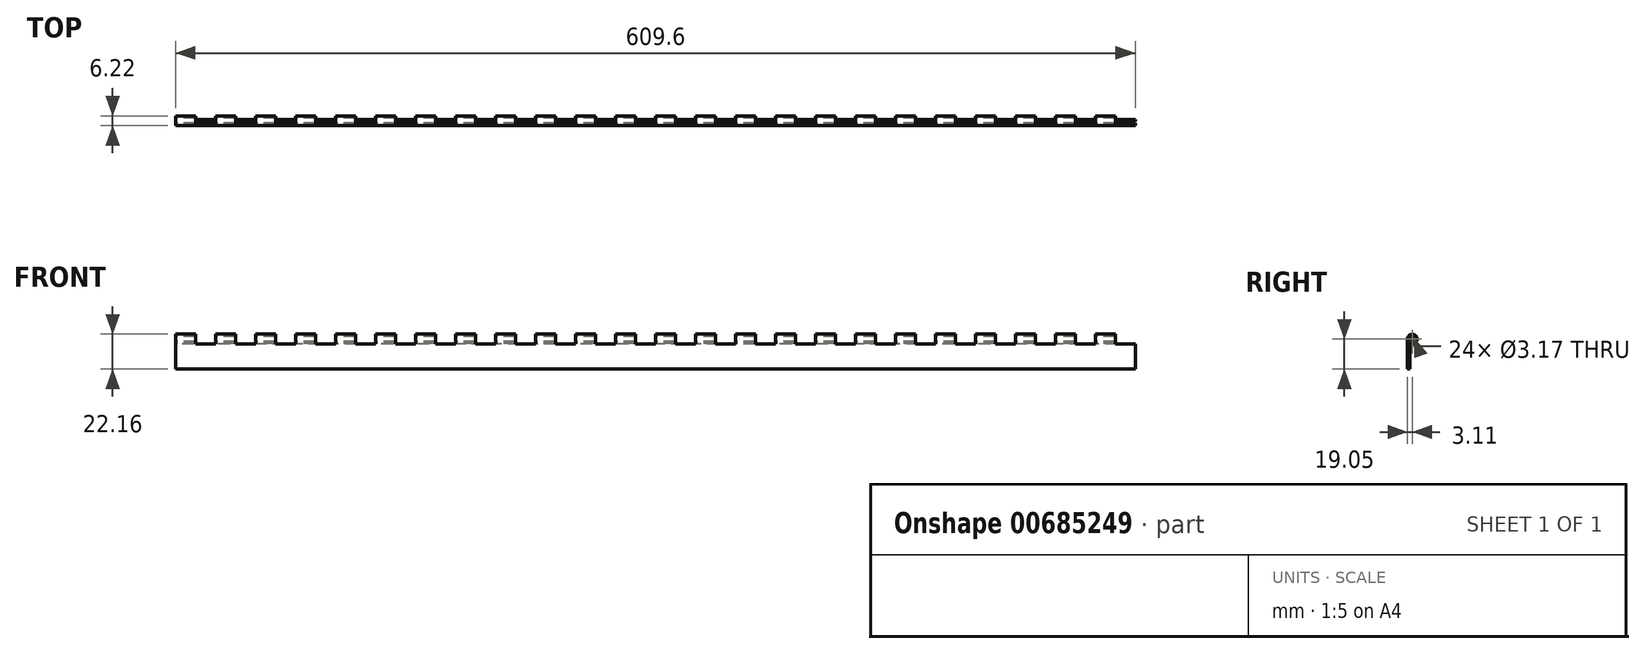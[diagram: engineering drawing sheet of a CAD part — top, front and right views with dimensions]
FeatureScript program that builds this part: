
annotation { "Feature Type Name" : "Feature", "Feature Type Description" : "" }
export const myFeature = defineFeature(function(context is Context, id is Id, definition is map)
    precondition{}
    {
        {
            var Q0;
            Q0=qCreatedBy(makeId("Right.planeOp"),FACE);
            var sketch = newSketch(context, id + "F0", { "sketchPlane" : qUnion([Q0])});
            skCircle(sketch, "E0", {"center": v(0, 0) * mm, "radius": 1.59 * mm});
            skArc(sketch, "E1", {"start": v(-1.59, -2.68) * mm, "mid": v(2.7, 1.54) * mm, "end": v(-3.11, 0) * mm});
            skLineSegment(sketch, "E2.top", {"start": v(-3.11, -19.05) * mm, "end": v(-1.59, -19.05) * mm});
            skLineSegment(sketch, "E2.left", {"start": v(-3.11, 0) * mm, "end": v(-3.11, -19.05) * mm});
            skLineSegment(sketch, "E2.right", {"start": v(-1.59, -2.68) * mm, "end": v(-1.59, -19.05) * mm});
            skSolve(sketch);
        }
        {
            var Q0;
            Q0 = qSketchRegion(id + "F0", true);
            extrude(context, id + "F1", {"entities" : qUnion([Q0]), "depth" : 609.6 * mm, "offsetDistance" : 25.4 * mm});
        }
        {
            var Q0;
            Q0=qCreatedBy(makeId("Front.planeOp"),FACE);
            var sketch = newSketch(context, id + "F2", { "sketchPlane" : qUnion([Q0])});
            skLineSegment(sketch, "E3.bottom", {"start": v(12.7, 3.18) * mm, "end": v(25.4, 3.18) * mm});
            skLineSegment(sketch, "E3.top", {"start": v(12.7, -3.05) * mm, "end": v(25.4, -3.05) * mm});
            skLineSegment(sketch, "E3.left", {"start": v(12.7, 3.18) * mm, "end": v(12.7, -3.05) * mm});
            skLineSegment(sketch, "E3.right", {"start": v(25.4, 3.18) * mm, "end": v(25.4, -3.05) * mm});
            skLineSegment(sketch, "E4.1.0.0", {"start": v(38.1, 3.18) * mm, "end": v(50.8, 3.18) * mm});
            skLineSegment(sketch, "E4.1.0.1", {"start": v(50.8, 3.18) * mm, "end": v(50.8, -3.05) * mm});
            skLineSegment(sketch, "E4.1.0.2", {"start": v(38.1, -3.05) * mm, "end": v(50.8, -3.05) * mm});
            skLineSegment(sketch, "E4.1.0.3", {"start": v(38.1, 3.18) * mm, "end": v(38.1, -3.05) * mm});
            skLineSegment(sketch, "E4.2.0.0", {"start": v(63.5, 3.18) * mm, "end": v(76.2, 3.18) * mm});
            skLineSegment(sketch, "E4.2.0.1", {"start": v(76.2, 3.18) * mm, "end": v(76.2, -3.05) * mm});
            skLineSegment(sketch, "E4.2.0.2", {"start": v(63.5, -3.05) * mm, "end": v(76.2, -3.05) * mm});
            skLineSegment(sketch, "E4.2.0.3", {"start": v(63.5, 3.18) * mm, "end": v(63.5, -3.05) * mm});
            skLineSegment(sketch, "E4.3.0.0", {"start": v(88.9, 3.18) * mm, "end": v(101.6, 3.18) * mm});
            skLineSegment(sketch, "E4.3.0.1", {"start": v(101.6, 3.18) * mm, "end": v(101.6, -3.05) * mm});
            skLineSegment(sketch, "E4.3.0.2", {"start": v(88.9, -3.05) * mm, "end": v(101.6, -3.05) * mm});
            skLineSegment(sketch, "E4.3.0.3", {"start": v(88.9, 3.18) * mm, "end": v(88.9, -3.05) * mm});
            skLineSegment(sketch, "E4.4.0.0", {"start": v(114.3, 3.18) * mm, "end": v(127, 3.18) * mm});
            skLineSegment(sketch, "E4.4.0.1", {"start": v(127, 3.18) * mm, "end": v(127, -3.05) * mm});
            skLineSegment(sketch, "E4.4.0.2", {"start": v(114.3, -3.05) * mm, "end": v(127, -3.05) * mm});
            skLineSegment(sketch, "E4.4.0.3", {"start": v(114.3, 3.18) * mm, "end": v(114.3, -3.05) * mm});
            skLineSegment(sketch, "E4.5.0.0", {"start": v(139.7, 3.18) * mm, "end": v(152.4, 3.18) * mm});
            skLineSegment(sketch, "E4.5.0.1", {"start": v(152.4, 3.18) * mm, "end": v(152.4, -3.05) * mm});
            skLineSegment(sketch, "E4.5.0.2", {"start": v(139.7, -3.05) * mm, "end": v(152.4, -3.05) * mm});
            skLineSegment(sketch, "E4.5.0.3", {"start": v(139.7, 3.18) * mm, "end": v(139.7, -3.05) * mm});
            skLineSegment(sketch, "E4.6.0.0", {"start": v(165.1, 3.18) * mm, "end": v(177.8, 3.18) * mm});
            skLineSegment(sketch, "E4.6.0.1", {"start": v(177.8, 3.18) * mm, "end": v(177.8, -3.05) * mm});
            skLineSegment(sketch, "E4.6.0.2", {"start": v(165.1, -3.05) * mm, "end": v(177.8, -3.05) * mm});
            skLineSegment(sketch, "E4.6.0.3", {"start": v(165.1, 3.18) * mm, "end": v(165.1, -3.05) * mm});
            skLineSegment(sketch, "E4.7.0.0", {"start": v(190.5, 3.18) * mm, "end": v(203.2, 3.18) * mm});
            skLineSegment(sketch, "E4.7.0.1", {"start": v(203.2, 3.18) * mm, "end": v(203.2, -3.05) * mm});
            skLineSegment(sketch, "E4.7.0.2", {"start": v(190.5, -3.05) * mm, "end": v(203.2, -3.05) * mm});
            skLineSegment(sketch, "E4.7.0.3", {"start": v(190.5, 3.18) * mm, "end": v(190.5, -3.05) * mm});
            skLineSegment(sketch, "E4.8.0.0", {"start": v(215.9, 3.18) * mm, "end": v(228.6, 3.18) * mm});
            skLineSegment(sketch, "E4.8.0.1", {"start": v(228.6, 3.18) * mm, "end": v(228.6, -3.05) * mm});
            skLineSegment(sketch, "E4.8.0.2", {"start": v(215.9, -3.05) * mm, "end": v(228.6, -3.05) * mm});
            skLineSegment(sketch, "E4.8.0.3", {"start": v(215.9, 3.18) * mm, "end": v(215.9, -3.05) * mm});
            skLineSegment(sketch, "E4.9.0.0", {"start": v(241.3, 3.18) * mm, "end": v(254, 3.18) * mm});
            skLineSegment(sketch, "E4.9.0.1", {"start": v(254, 3.18) * mm, "end": v(254, -3.05) * mm});
            skLineSegment(sketch, "E4.9.0.2", {"start": v(241.3, -3.05) * mm, "end": v(254, -3.05) * mm});
            skLineSegment(sketch, "E4.9.0.3", {"start": v(241.3, 3.18) * mm, "end": v(241.3, -3.05) * mm});
            skLineSegment(sketch, "E4.10.0.0", {"start": v(266.7, 3.18) * mm, "end": v(279.4, 3.18) * mm});
            skLineSegment(sketch, "E4.10.0.1", {"start": v(279.4, 3.18) * mm, "end": v(279.4, -3.05) * mm});
            skLineSegment(sketch, "E4.10.0.2", {"start": v(266.7, -3.05) * mm, "end": v(279.4, -3.05) * mm});
            skLineSegment(sketch, "E4.10.0.3", {"start": v(266.7, 3.18) * mm, "end": v(266.7, -3.05) * mm});
            skLineSegment(sketch, "E4.11.0.0", {"start": v(292.1, 3.18) * mm, "end": v(304.8, 3.18) * mm});
            skLineSegment(sketch, "E4.11.0.1", {"start": v(304.8, 3.18) * mm, "end": v(304.8, -3.05) * mm});
            skLineSegment(sketch, "E4.11.0.2", {"start": v(292.1, -3.05) * mm, "end": v(304.8, -3.05) * mm});
            skLineSegment(sketch, "E4.11.0.3", {"start": v(292.1, 3.18) * mm, "end": v(292.1, -3.05) * mm});
            skLineSegment(sketch, "E4.12.0.0", {"start": v(317.5, 3.18) * mm, "end": v(330.2, 3.18) * mm});
            skLineSegment(sketch, "E4.12.0.1", {"start": v(330.2, 3.18) * mm, "end": v(330.2, -3.05) * mm});
            skLineSegment(sketch, "E4.12.0.2", {"start": v(317.5, -3.05) * mm, "end": v(330.2, -3.05) * mm});
            skLineSegment(sketch, "E4.12.0.3", {"start": v(317.5, 3.18) * mm, "end": v(317.5, -3.05) * mm});
            skLineSegment(sketch, "E4.13.0.0", {"start": v(342.9, 3.18) * mm, "end": v(355.6, 3.18) * mm});
            skLineSegment(sketch, "E4.13.0.1", {"start": v(355.6, 3.18) * mm, "end": v(355.6, -3.05) * mm});
            skLineSegment(sketch, "E4.13.0.2", {"start": v(342.9, -3.05) * mm, "end": v(355.6, -3.05) * mm});
            skLineSegment(sketch, "E4.13.0.3", {"start": v(342.9, 3.18) * mm, "end": v(342.9, -3.05) * mm});
            skLineSegment(sketch, "E4.14.0.0", {"start": v(368.3, 3.18) * mm, "end": v(381, 3.18) * mm});
            skLineSegment(sketch, "E4.14.0.1", {"start": v(381, 3.18) * mm, "end": v(381, -3.05) * mm});
            skLineSegment(sketch, "E4.14.0.2", {"start": v(368.3, -3.05) * mm, "end": v(381, -3.05) * mm});
            skLineSegment(sketch, "E4.14.0.3", {"start": v(368.3, 3.18) * mm, "end": v(368.3, -3.05) * mm});
            skLineSegment(sketch, "E4.15.0.0", {"start": v(393.7, 3.18) * mm, "end": v(406.4, 3.18) * mm});
            skLineSegment(sketch, "E4.15.0.1", {"start": v(406.4, 3.18) * mm, "end": v(406.4, -3.05) * mm});
            skLineSegment(sketch, "E4.15.0.2", {"start": v(393.7, -3.05) * mm, "end": v(406.4, -3.05) * mm});
            skLineSegment(sketch, "E4.15.0.3", {"start": v(393.7, 3.18) * mm, "end": v(393.7, -3.05) * mm});
            skLineSegment(sketch, "E4.16.0.0", {"start": v(419.1, 3.18) * mm, "end": v(431.8, 3.18) * mm});
            skLineSegment(sketch, "E4.16.0.1", {"start": v(431.8, 3.18) * mm, "end": v(431.8, -3.05) * mm});
            skLineSegment(sketch, "E4.16.0.2", {"start": v(419.1, -3.05) * mm, "end": v(431.8, -3.05) * mm});
            skLineSegment(sketch, "E4.16.0.3", {"start": v(419.1, 3.18) * mm, "end": v(419.1, -3.05) * mm});
            skLineSegment(sketch, "E4.17.0.0", {"start": v(444.5, 3.18) * mm, "end": v(457.2, 3.18) * mm});
            skLineSegment(sketch, "E4.17.0.1", {"start": v(457.2, 3.18) * mm, "end": v(457.2, -3.05) * mm});
            skLineSegment(sketch, "E4.17.0.2", {"start": v(444.5, -3.05) * mm, "end": v(457.2, -3.05) * mm});
            skLineSegment(sketch, "E4.17.0.3", {"start": v(444.5, 3.18) * mm, "end": v(444.5, -3.05) * mm});
            skLineSegment(sketch, "E4.18.0.0", {"start": v(469.9, 3.18) * mm, "end": v(482.6, 3.18) * mm});
            skLineSegment(sketch, "E4.18.0.1", {"start": v(482.6, 3.18) * mm, "end": v(482.6, -3.05) * mm});
            skLineSegment(sketch, "E4.18.0.2", {"start": v(469.9, -3.05) * mm, "end": v(482.6, -3.05) * mm});
            skLineSegment(sketch, "E4.18.0.3", {"start": v(469.9, 3.18) * mm, "end": v(469.9, -3.05) * mm});
            skLineSegment(sketch, "E4.19.0.0", {"start": v(495.3, 3.18) * mm, "end": v(508, 3.18) * mm});
            skLineSegment(sketch, "E4.19.0.1", {"start": v(508, 3.18) * mm, "end": v(508, -3.05) * mm});
            skLineSegment(sketch, "E4.19.0.2", {"start": v(495.3, -3.05) * mm, "end": v(508, -3.05) * mm});
            skLineSegment(sketch, "E4.19.0.3", {"start": v(495.3, 3.18) * mm, "end": v(495.3, -3.05) * mm});
            skLineSegment(sketch, "E4.20.0.0", {"start": v(520.7, 3.18) * mm, "end": v(533.4, 3.18) * mm});
            skLineSegment(sketch, "E4.20.0.1", {"start": v(533.4, 3.18) * mm, "end": v(533.4, -3.05) * mm});
            skLineSegment(sketch, "E4.20.0.2", {"start": v(520.7, -3.05) * mm, "end": v(533.4, -3.05) * mm});
            skLineSegment(sketch, "E4.20.0.3", {"start": v(520.7, 3.18) * mm, "end": v(520.7, -3.05) * mm});
            skLineSegment(sketch, "E4.21.0.0", {"start": v(546.1, 3.18) * mm, "end": v(558.8, 3.18) * mm});
            skLineSegment(sketch, "E4.21.0.1", {"start": v(558.8, 3.18) * mm, "end": v(558.8, -3.05) * mm});
            skLineSegment(sketch, "E4.21.0.2", {"start": v(546.1, -3.05) * mm, "end": v(558.8, -3.05) * mm});
            skLineSegment(sketch, "E4.21.0.3", {"start": v(546.1, 3.18) * mm, "end": v(546.1, -3.05) * mm});
            skLineSegment(sketch, "E4.22.0.0", {"start": v(571.5, 3.18) * mm, "end": v(584.2, 3.18) * mm});
            skLineSegment(sketch, "E4.22.0.1", {"start": v(584.2, 3.18) * mm, "end": v(584.2, -3.05) * mm});
            skLineSegment(sketch, "E4.22.0.2", {"start": v(571.5, -3.05) * mm, "end": v(584.2, -3.05) * mm});
            skLineSegment(sketch, "E4.22.0.3", {"start": v(571.5, 3.18) * mm, "end": v(571.5, -3.05) * mm});
            skLineSegment(sketch, "E4.23.0.0", {"start": v(596.9, 3.18) * mm, "end": v(609.6, 3.18) * mm});
            skLineSegment(sketch, "E4.23.0.1", {"start": v(609.6, 3.18) * mm, "end": v(609.6, -3.05) * mm});
            skLineSegment(sketch, "E4.23.0.2", {"start": v(596.9, -3.05) * mm, "end": v(609.6, -3.05) * mm});
            skLineSegment(sketch, "E4.23.0.3", {"start": v(596.9, 3.18) * mm, "end": v(596.9, -3.05) * mm});
            skLineSegment(sketch, "E4.direction1", {"start": v(12.7, 3.18) * mm, "end": v(38.1, 3.18) * mm, "construction": true});
            skSolve(sketch);
        }
        {
            var Q0;
            Q0 = qSketchRegion(id + "F2", true);
            extrude(context, id + "F3", {"entities" : qUnion([Q0]), "operationType" : NewBodyOperationType.REMOVE, "oppositeDirection" : true, "depth" : 25.4 * mm, "offsetDistance" : 25.4 * mm, "hasSecondDirection" : true, "secondDirectionOppositeDirection" : false, "secondDirectionDepth" : 25.4 * mm});
        }
    });
